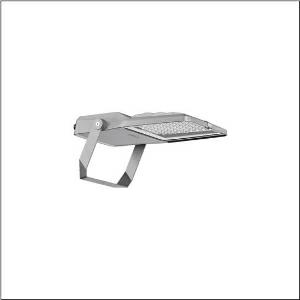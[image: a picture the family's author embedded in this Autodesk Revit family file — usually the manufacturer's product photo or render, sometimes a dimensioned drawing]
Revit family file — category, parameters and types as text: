
# Revit family: floodlight_fl_21_iq_mini___pl61_5xa7772b2c1a_d28a
name_source: partatom
category: Lighting Fixtures
units: mm (PartAtom-declared; Revit-internal decimal feet)

## family parameters
Cut with Voids When Loaded = No
Host = Face
Light Source = No
Part Type = Normal
Room Calculation Point = No
Round Connector Dimension = Use Diameter
Shared = No

## types (1)
- --- (1 x LED, 6120 lm, 45.5 W, 3000K)
    Apparent Load = 46 VA
    CIE Flux Codes = 33 65 98 100 100
    Color Rendering = 70
    Color Temperature = 3000K
    Default Elevation = 1800 mm
    Description = Floodlight FL 21 iQ mini, floodlight, primary light control with lens, of PMMA, primary optical cover: protective disc, of toughened safety glass, transparent, light distribution: PL61, light emission: direct distribution, installation type: surface-mounted, LED, High Power LED, rated luminous flux: 6.120lm, luminous efficacy: 135lm/W, light colour: 730, colour temperature: 3000K, control gear: iQ Street-Remote/DALI, control: Street-Remote, Auto-Match, Temp-Guard, Night-Set, Smart-Wire, Desk-Remote (wireless, voltage-free reading and setting of iQ features in the workshop via application-optimized NFC function/RFID function), optimised constant luminous flux control (CLO 2.0), with terminal, 6-pole, mains connection: 220..240V, AC, 50/60Hz, start of lifetime: 46W, end of service life: 48W, reduction: 22W, luminaire housing, of diecast aluminium, powder-coated, Siteco® metallic grey (DB 702S), corrosivity category C5 mid according to DIN EN ISO 12944, suitable for swimming pools, chlorine-resistant, sealing non-destructively replaceable, mounting bracket, of steel, galvanised, powder-coated, Siteco® metallic grey (DB 702S), protection rating (complete): IP66, insulation class (complete): insulation class II (safety insulation), certification: CE, ENEC, VDE, protection symbol: D, impact resistance: IK08, permissible operating ambient temperature: -40..+40°C, permissible operating ambient temperature for outdoor applications: -40..+50°C, standard: DIN EN 12944, LABS conformity tested according to VDMA 24364:2018-05, packaging unit: 1 piece

Light Distribution: PL61
    Height = 70 mm
    Lamp = 1 x LED
    Lamp Light Flux = 6120 lm
    Lamp Power = 45.5 W
    Lamp count = 1
    Length = 485 mm
    Luminous efficacy = 135 lm/W
    Manufacturer = Siteco
    ModVariant = No
    Model = 5XA7772B2C1A
    Number of Poles = 1
    OnlyDefault = Yes
    Power Factor = 1
    Product Name = Floodlight FL 21 iQ mini | PL61
    Product group = floodlight | pylon annexe
    ProductGroupID = 6200
    Protection Class = Protection class II
    Protection Degree = IP 66
    RLX_Detail_Level = 1
    RLX_Emergency_Light_Flux = 0 lm
    RLX_Emergency_Type = 0
    RLX_Emergency_Type_DB = No
    RlxData = <blob elided: 96405 chars, md5=cdc1266b>
    Socket = socket
    Standby Power = 0 W
    System Light Flux = 6120 lm
    System Power = 46 W
    Type Comments = factory setting: luminous flux: 100 % | dim-lin: 254 | 463 mA
    Type Image = l_1006845.jpg
    URL = http://relux.com
    VarID = @adj_173656
    Voltage = 0 V
    Weight = 0.00 kg
    Width = 337 mm

## geometry (parser evidence)
native form markers: Blend x4, Sweep x11
no freeform markers — native parametric forms only
